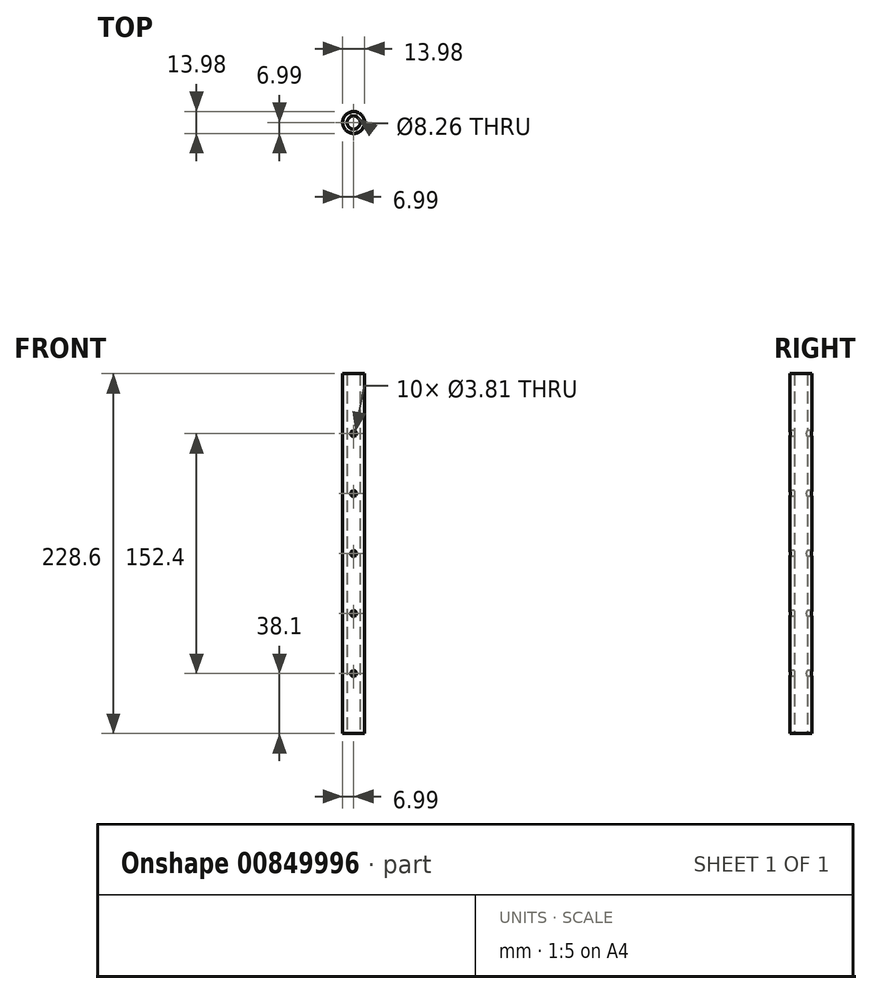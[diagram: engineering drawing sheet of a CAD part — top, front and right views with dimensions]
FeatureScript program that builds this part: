
annotation { "Feature Type Name" : "Feature", "Feature Type Description" : "" }
export const myFeature = defineFeature(function(context is Context, id is Id, definition is map)
    precondition{}
    {
        {
            var Q0;
            Q0=qCreatedBy(makeId("Top.planeOp"),FACE);
            var sketch = newSketch(context, id + "F0", { "sketchPlane" : qUnion([Q0])});
            skCircle(sketch, "E0", {"center": v(0, 0) * mm, "radius": 4.13 * mm});
            skCircle(sketch, "E1", {"center": v(0, 0) * mm, "radius": 6.99 * mm});
            skSolve(sketch);
        }
        {
            var Q0;
            Q0=makeQuery(id+"F0.imprint","IMPRINT",FACE,{"disambiguationData":[TD([[makeQuery(id+"F0.imprint","IMPRINT",EDGE,{"derivedFrom":sQuery(id+"F0.wireOp",EDGE,"E0")}),-1.0]])]});
            extrude(context, id + "F1", {"entities" : qUnion([Q0]), "depth" : 228.6 * mm, "offsetDistance" : 25.4 * mm});
        }
        {
            var Q0;
            Q0=qCreatedBy(makeId("Front.planeOp"),FACE);
            var sketch = newSketch(context, id + "F2", { "sketchPlane" : qUnion([Q0])});
            skCircle(sketch, "E2", {"center": v(0, 38.1) * mm, "radius": 1.9 * mm});
            skCircle(sketch, "E3.0.1.0", {"center": v(0, 76.2) * mm, "radius": 1.9 * mm});
            skCircle(sketch, "E3.0.2.0", {"center": v(0, 114.3) * mm, "radius": 1.9 * mm});
            skCircle(sketch, "E3.0.3.0", {"center": v(0, 152.4) * mm, "radius": 1.9 * mm});
            skCircle(sketch, "E3.0.4.0", {"center": v(0, 190.5) * mm, "radius": 1.9 * mm});
            skLineSegment(sketch, "E3.direction1", {"start": v(0, 38.1) * mm, "end": v(25.4, 38.1) * mm, "construction": true});
            skLineSegment(sketch, "E3.direction2", {"start": v(0, 38.1) * mm, "end": v(0, 76.2) * mm, "construction": true});
            skSolve(sketch);
        }
        {
            var Q0;
            Q0 = qSketchRegion(id + "F2", true);
            extrude(context, id + "F3", {"entities" : qUnion([Q0]), "operationType" : NewBodyOperationType.REMOVE, "oppositeDirection" : true, "depth" : 25.4 * mm, "offsetDistance" : 25.4 * mm, "hasSecondDirection" : true, "secondDirectionOppositeDirection" : false, "secondDirectionDepth" : 25.4 * mm});
        }
    });
